# Revit family: NBS_TapcoRoofingProducts_RcnstttdSltCrsngFitngs_TapcoSlate_ClassicRidgeToHipJunction
name_source: partatom
category: Generic Models
units: mm (PartAtom-declared; Revit-internal decimal feet)

## family parameters
Can host rebar = No
Cut with Voids When Loaded = No
Part Type = Normal
Room Calculation Point = No
Round Connector Dimension = Use Diameter
Shared = No

## types (21) — shared parameters
Applications = Suitable for Tapco Slate Classic and Tapco Slate Classic Ridge and Hip Caps, it is especially valuable for the 3-way junction on an Edwardian conservatory roof
AssetType = Fixed
Category = Pr_25_93_72_73:Reconstituted slate coursing fittings
ClassicRidgeEndCapMaterial = NBS_TapcoRoofingProducts_Slate_804PewterGrey
ClassicRidgeEndCapWidth = 268 mm  [stored 0.879265 ft]
CodePerformance = Fully tested to BBA, ETA and CE standards
Combustible = Yes
Description = A dry-fix ridge to hip junction cap for all roofs where the ridge meets the hip
DurationUnit = year
ExpectedLife = 80+ years
Features = Lightweight – as low as 12 kg per square metre, easy to install with pre-marked nailing guides and spacers, easily cut with a fine-toothed saw or sharp utility blade, mechanically fixed
FireRating = BS476 Part 3, Boarded Roof SAA, Battened Roof SAC
FlammabilityRating = BS476 Part 3, Boarded Roof SAA, Battened Roof SAC
IfcExportAs = IfcCoveringType
IfcExportType = ROOFING
IsExternal = Yes
ManufacturerName = Tapco Roofing Products
ManufacturerURL = www.tapcoroofingproducts.com
Material = Virgin limestone, polypropylene
NBSCertification = www.nationalbimlibrary.com/cert/s0vwkabx
NBSDescription = Reconstituted slates coursing fittings
NBSReference = 45-80-90/388
NominalHeight = 45 mm
NominalLength = 445 mm  [stored 1.45997 ft]
NominalWidth = 300 mm
ProductInformation = https://www.tapcoroofingproducts.com
Shape = Rectangular
Size = 14 x 445 x 300 mm
Status = UNSET
Uniclass2015Code = Pr_25_93_72_73
Uniclass2015Title = Reconstituted slate coursing fittings
Uniclass2015Version = Products v1.20
Version = 1
WarrantyDescription = 40-years
WarrantyDurationUnit = year
zero-valued in all types: ThermalTransmittance

## per-type parameters (varying)
| type | BIMObjectName | Color | Colour | EndCapPitchAngle | ModelNumber | Name | PitchRange |
| TapcoSlate_ClassicRidgeToHipJunction_801StoneBlack_14To17DegPitch | NBS_TapcoRoofingProducts_ReconstitutedSlatesCoursingFittings_TapcoSlate_ClassicRidgeToHipJunction_801StoneBlack_14To17DegPitch | Stone black | Stone black | 14.00° | 801 | ReconstitutedSlatesCoursingFittings_TapcoSlate_ClassicRidgeToHipJunction_801StoneBlack_14To17DegPitch_TapcoRoofingProducts | 14° - 17° |
| TapcoSlate_ClassicRidgeToHipJunction_801StoneBlack_18To24DegPitch | NBS_TapcoRoofingProducts_ReconstitutedSlatesCoursingFittings_TapcoSlate_ClassicRidgeToHipJunction_801StoneBlack_18To24DegPitch | Stone black | Stone black | 18.00° | 801 | ReconstitutedSlatesCoursingFittings_TapcoSlate_ClassicRidgeToHipJunction_801StoneBlack_18To24DegPitch_TapcoRoofingProducts | 18° - 24° |
| TapcoSlate_ClassicRidgeToHipJunction_801StoneBlack_25To30DegPitch | NBS_TapcoRoofingProducts_ReconstitutedSlatesCoursingFittings_TapcoSlate_ClassicRidgeToHipJunction_801StoneBlack_25To30DegPitch | Stone black | Stone black | 25.00° | 801 | ReconstitutedSlatesCoursingFittings_TapcoSlate_ClassicRidgeToHipJunction_801StoneBlack_25To30DegPitch_TapcoRoofingProducts | 25° - 30° |
| TapcoSlate_ClassicRidgeToHipJunction_804PewterGrey_14To17DegPitch | NBS_TapcoRoofingProducts_ReconstitutedSlatesCoursingFittings_TapcoSlate_ClassicRidgeToHipJunction_804PewterGrey_14To17DegPitch | Pewter grey | Pewter grey | 14.00° | 804 | ReconstitutedSlatesCoursingFittings_TapcoSlate_ClassicRidgeToHipJunction_804PewterGrey_14To17DegPitch_TapcoRoofingProducts | 14° - 17° |
| TapcoSlate_ClassicRidgeToHipJunction_804PewterGrey_18To24DegPitch | NBS_TapcoRoofingProducts_ReconstitutedSlatesCoursingFittings_TapcoSlate_ClassicRidgeToHipJunction_804PewterGrey_18To24DegPitch | Pewter grey | Pewter grey | 18.00° | 804 | ReconstitutedSlatesCoursingFittings_TapcoSlate_ClassicRidgeToHipJunction_804PewterGrey_18To24DegPitch_TapcoRoofingProducts | 18° - 24° |
| TapcoSlate_ClassicRidgeToHipJunction_804PewterGrey_25To30DegPitch | NBS_TapcoRoofingProducts_ReconstitutedSlatesCoursingFittings_TapcoSlate_ClassicRidgeToHipJunction_804PewterGrey_25To30DegPitch | Pewter grey | Pewter grey | 25.00° | 804 | ReconstitutedSlatesCoursingFittings_TapcoSlate_ClassicRidgeToHipJunction_804PewterGrey_25To30DegPitch_TapcoRoofingProducts | 25° - 30° |
| TapcoSlate_ClassicRidgeToHipJunction_809RedRock_14To17DegPitch | NBS_TapcoRoofingProducts_ReconstitutedSlatesCoursingFittings_TapcoSlate_ClassicRidgeToHipJunction_809RedRock_14To17DegPitch | Red rock | Red rock | 14.00° | 809 | ReconstitutedSlatesCoursingFittings_TapcoSlate_ClassicRidgeToHipJunction_809RedRock_14To17DegPitch_TapcoRoofingProducts | 14° - 17° |
| TapcoSlate_ClassicRidgeToHipJunction_809RedRock_18To24DegPitch | NBS_TapcoRoofingProducts_ReconstitutedSlatesCoursingFittings_TapcoSlate_ClassicRidgeToHipJunction_809RedRock_18To24DegPitch | Red rock | Red rock | 18.00° | 809 | ReconstitutedSlatesCoursingFittings_TapcoSlate_ClassicRidgeToHipJunction_809RedRock_18To24DegPitch_TapcoRoofingProducts | 18° - 24° |
| TapcoSlate_ClassicRidgeToHipJunction_809RedRock_25To30DegPitch | NBS_TapcoRoofingProducts_ReconstitutedSlatesCoursingFittings_TapcoSlate_ClassicRidgeToHipJunction_809RedRock_25To30DegPitch | Red rock | Red rock | 25.00° | 809 | ReconstitutedSlatesCoursingFittings_TapcoSlate_ClassicRidgeToHipJunction_809RedRock_25To30DegPitch_TapcoRoofingProducts | 25° - 30° |
| TapcoSlate_ClassicRidgeToHipJunction_706Plum_14To17DegPitch | NBS_TapcoRoofingProducts_ReconstitutedSlatesCoursingFittings_TapcoSlate_ClassicRidgeToHipJunction_706Plum_14To17DegPitch | Plum | Plum | 14.00° | 706 | ReconstitutedSlatesCoursingFittings_TapcoSlate_ClassicRidgeToHipJunction_706Plum_14To17DegPitch_TapcoRoofingProducts | 14° - 17° |
| TapcoSlate_ClassicRidgeToHipJunction_706Plum_18To24DegPitch | NBS_TapcoRoofingProducts_ReconstitutedSlatesCoursingFittings_TapcoSlate_ClassicRidgeToHipJunction_706Plum_18To24DegPitch | Plum | Plum | 18.00° | 706 | ReconstitutedSlatesCoursingFittings_TapcoSlate_ClassicRidgeToHipJunction_706Plum_18To24DegPitch_TapcoRoofingProducts | 18° - 24° |
| TapcoSlate_ClassicRidgeToHipJunction_706Plum_25To30DegPitch | NBS_TapcoRoofingProducts_ReconstitutedSlatesCoursingFittings_TapcoSlate_ClassicRidgeToHipJunction_706Plum_25To30DegPitch | Plum | Plum | 25.00° | 706 | ReconstitutedSlatesCoursingFittings_TapcoSlate_ClassicRidgeToHipJunction_706Plum_25To30DegPitch_TapcoRoofingProducts | 25° - 30° |
| TapcoSlate_ClassicRidgeToHipJunction_709BrickRed_14To17DegPitch | NBS_TapcoRoofingProducts_ReconstitutedSlatesCoursingFittings_TapcoSlate_ClassicRidgeToHipJunction_709BrickRed_14To17DegPitch | Brick red | Brick red | 14.00° | 709 | ReconstitutedSlatesCoursingFittings_TapcoSlate_ClassicRidgeToHipJunction_709BrickRed_14To17DegPitch_TapcoRoofingProducts | 14° - 17° |
| TapcoSlate_ClassicRidgeToHipJunction_709BrickRed_18To24DegPitch | NBS_TapcoRoofingProducts_ReconstitutedSlatesCoursingFittings_TapcoSlate_ClassicRidgeToHipJunction_709BrickRed_18To24DegPitch | Brick red | Brick red | 18.00° | 709 | ReconstitutedSlatesCoursingFittings_TapcoSlate_ClassicRidgeToHipJunction_709BrickRed_18To24DegPitch_TapcoRoofingProducts | 18° - 24° |
| TapcoSlate_ClassicRidgeToHipJunction_709BrickRed_25To30DegPitch | NBS_TapcoRoofingProducts_ReconstitutedSlatesCoursingFittings_TapcoSlate_ClassicRidgeToHipJunction_709BrickRed_25To30DegPitch | Brick red | Brick red | 25.00° | 709 | ReconstitutedSlatesCoursingFittings_TapcoSlate_ClassicRidgeToHipJunction_709BrickRed_25To30DegPitch_TapcoRoofingProducts | 25° - 30° |
| TapcoSlate_ClassicRidgeToHipJunction_712ChestnutBrown_14To17DegPitch | NBS_TapcoRoofingProducts_ReconstitutedSlatesCoursingFittings_TapcoSlate_ClassicRidgeToHipJunction_712ChestnutBrown_14To17DegPitch | Chestnut brown | Chestnut brown | 14.00° | 712 | ReconstitutedSlatesCoursingFittings_TapcoSlate_ClassicRidgeToHipJunction_712ChestnutBrown_14To17DegPitch_TapcoRoofingProducts | 14° - 17° |
| TapcoSlate_ClassicRidgeToHipJunction_712ChestnutBrown_18To24DegPitch | NBS_TapcoRoofingProducts_ReconstitutedSlatesCoursingFittings_TapcoSlate_ClassicRidgeToHipJunction_712ChestnutBrown_18To24DegPitch | Chestnut brown | Chestnut brown | 18.00° | 712 | ReconstitutedSlatesCoursingFittings_TapcoSlate_ClassicRidgeToHipJunction_712ChestnutBrown_18To24DegPitch_TapcoRoofingProducts | 18° - 24° |
| TapcoSlate_ClassicRidgeToHipJunction_712ChestnutBrown_25To30DegPitch | NBS_TapcoRoofingProducts_ReconstitutedSlatesCoursingFittings_TapcoSlate_ClassicRidgeToHipJunction_712ChestnutBrown_25To30DegPitch | Chestnut brown | Chestnut brown | 25.00° | 712 | ReconstitutedSlatesCoursingFittings_TapcoSlate_ClassicRidgeToHipJunction_712ChestnutBrown_25To30DegPitch_TapcoRoofingProducts | 25° - 30° |
| TapcoSlate_ClassicRidgeToHipJunction_801StoneBlack_25To29DegPitch | NBS_TapcoRoofingProducts_ReconstitutedSlatesCoursingFittings_TapcoSlate_ClassicRidgeToHipJunction_801StoneBlack_25To29DegPitch | Stone black | Stone black | 25.00° | 801 | ReconstitutedSlatesCoursingFittings_TapcoSlate_ClassicRidgeToHipJunction_801StoneBlack_25To29DegPitch_TapcoRoofingProducts | 25° - 29° |
| TapcoSlate_ClassicRidgeToHipJunction_801StoneBlack_30To34DegPitch | NBS_TapcoRoofingProducts_ReconstitutedSlatesCoursingFittings_TapcoSlate_ClassicRidgeToHipJunction_801StoneBlack_30To34DegPitch | Stone black | Stone black | 30.00° | 801 | ReconstitutedSlatesCoursingFittings_TapcoSlate_ClassicRidgeToHipJunction_801StoneBlack_30To34DegPitch_TapcoRoofingProducts | 30° - 34° |
| TapcoSlate_ClassicRidgeToHipJunction_801StoneBlack_35To40DegPitch | NBS_TapcoRoofingProducts_ReconstitutedSlatesCoursingFittings_TapcoSlate_ClassicRidgeToHipJunction_801StoneBlack_35To40DegPitch | Stone black | Stone black | 35.00° | 801 | ReconstitutedSlatesCoursingFittings_TapcoSlate_ClassicRidgeToHipJunction_801StoneBlack_35To40DegPitch_TapcoRoofingProducts | 35° - 40° |

note: column(s) folded — value = type name in every type: ModelReference

note: [stored X ft] marks values corroborated as IEEE doubles in the binary element streams (Revit-internal decimal feet)

## geometry (parser evidence)
native form markers: Sweep x2
no freeform markers — native parametric forms only
